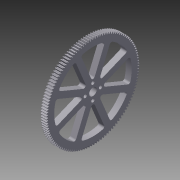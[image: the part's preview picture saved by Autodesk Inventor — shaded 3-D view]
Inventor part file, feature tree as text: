
AUTODESK INVENTOR PART (.ipt)
format: ipt  version: 2014 SP1 (Build 180222100, 222)  size: 830,464 bytes
history: native  units: in
note: dims shown in document units (in); Inventor stores cm internally (conversion verified against a paired STEP export)
features: imported_body x1, extrude x1, fillet x1, pattern_circular x1, sketch x1
ambient origin geometry x8: Origin, YZ Plane, XZ Plane, XY Plane, X Axis, Y Axis, Z Axis, Center Point
bodies: Solid1 (feature_tree)
feature tree (5):
  imported_body  "Base1"
  extrude  "Extrusion1"  Depth=0.0787in
  fillet  "Fillet1"  [1 undecoded]
  pattern_circular  "Circular Pattern1"  Angle=22.5deg  [1 undecoded]
  sketch  "Sketch1"  dims[d1=0.25in d10=0.0787in d11=22.5deg d12=22.5deg d13=0.6404in d14=0.3937in d15=0.0in d16=0.0787in d17=3.1496in d18=360.0deg]
note: 2 required parameter values undecoded (feature->parameter linkage not recoverable at this tier; creation-order binding heuristic only, values carry confidence <= 0.55)
